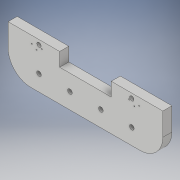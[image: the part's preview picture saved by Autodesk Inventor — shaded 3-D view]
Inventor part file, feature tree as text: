
AUTODESK INVENTOR PART (.ipt)
format: ipt  version: 2019 (Build 230136000, 136)  size: 171,008 bytes
history: native  units: in
note: dims shown in document units (in); Inventor stores cm internally (conversion verified against a paired STEP export)
features: sketch x5, hole x3, extrude x2
ambient origin geometry x8: Origin, YZ Plane, XZ Plane, XY Plane, X Axis, Y Axis, Z Axis, Center Point
bodies: Solid1 (feature_tree)
feature tree (10):
  extrude  "Extrusion1"  Depth=3.5in
  hole  "Hole1"  [1 undecoded]
  extrude  "Extrusion2"  Depth=3.5in
  hole  "Hole2"  [1 undecoded]
  hole  "Hole3"  [1 undecoded]
  sketch  "Sketch1"  dims[d0=17.0in d1=3.5in]
  sketch  "Sketch2"  dims[d2=2.5in d3=2.5in]
  sketch  "Sketch3"  dims[d4=1.0in d5=0.0in d6=3.5in]
  sketch  "Sketch4"  dims[d7=1.75in d8=1.75in]
  sketch  "Sketch5"  dims[d9=1.75in d10=1.75in d11=17.0in d12=3.4in d13=6.8in d14=6.8in d15=3.4in d16=0.505in d17=0.75in d18=0.375in d19=0.25in d20=0.5635in d21=1.0in d22=0.8108in d27=17.0in d28=5.6667in d29=5.6667in d30=1.5in d31=0.0in d32=1.5in d33=1.5in d34=0.5in d35=0.5in d38=0.0in d39=0.0in d40=0.472in d41=0.75in d42=0.375in d43=0.25in d44=0.5635in d45=1.0in d46=0.8108in d47=0.305in d48=0.253in d49=0.276in d50=0.61in d51=0.804in d52=0.305in d53=0.305in d54=0.253in d55=0.61in d56=0.276in d57=0.305in d58=0.804in d59=0.125in d60=0.75in d61=0.375in d62=0.25in d63=0.5635in d64=1.0in d65=0.8108in]
note: 3 required parameter values undecoded (feature->parameter linkage not recoverable at this tier; creation-order binding heuristic only, values carry confidence <= 0.55)
